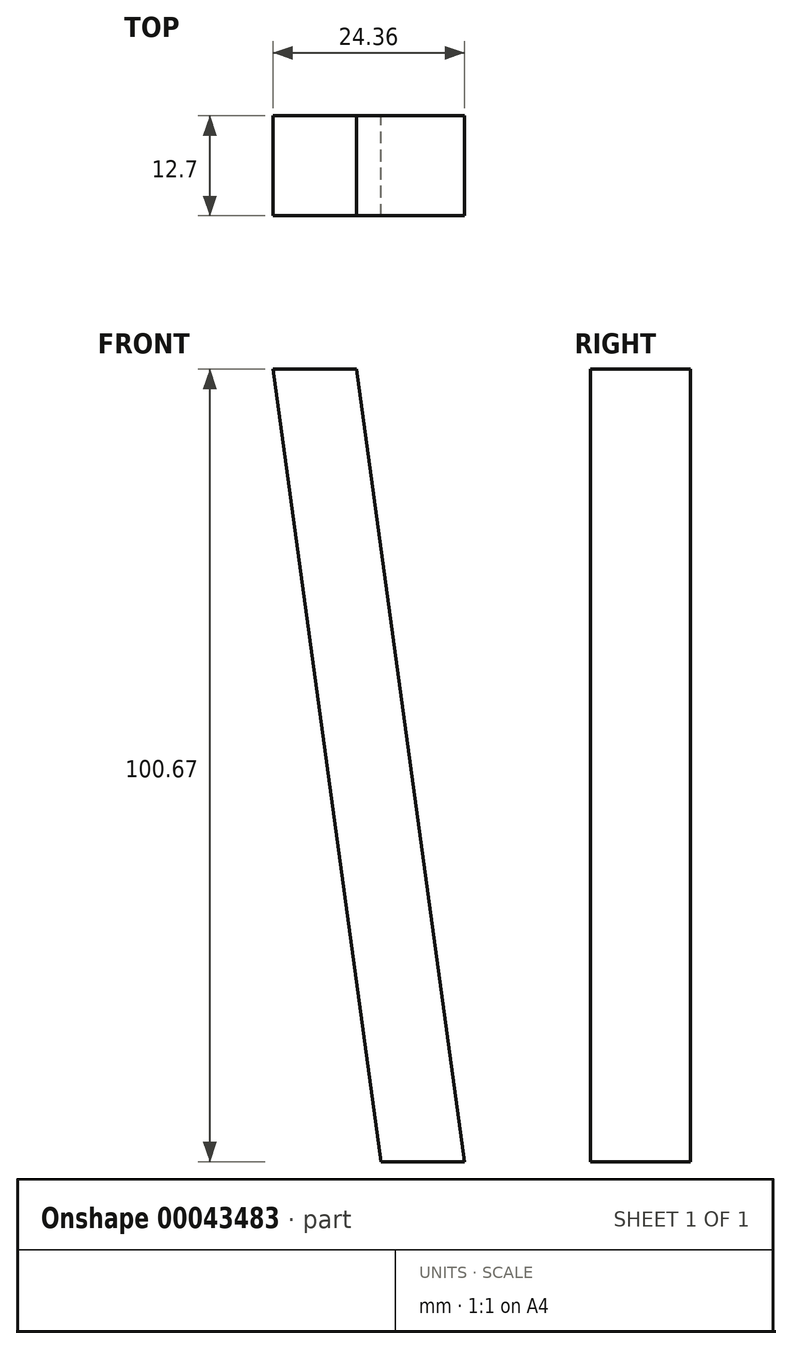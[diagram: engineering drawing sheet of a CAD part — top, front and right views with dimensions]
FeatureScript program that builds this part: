
annotation { "Feature Type Name" : "Feature", "Feature Type Description" : "" }
export const myFeature = defineFeature(function(context is Context, id is Id, definition is map)
    precondition{}
    {
        {
            var Q0;
            Q0=qCreatedBy(makeId("Front.planeOp"),FACE);
            var sketch = newSketch(context, id + "F0", { "sketchPlane" : qUnion([Q0])});
            skLineSegment(sketch, "E0", {"start": v(13.13, 55.6) * mm, "end": v(23.77, 55.6) * mm});
            skLineSegment(sketch, "E1", {"start": v(23.77, 55.6) * mm, "end": v(37.5, -45.06) * mm});
            skLineSegment(sketch, "E2", {"start": v(37.5, -45.06) * mm, "end": v(26.85, -45.06) * mm});
            skLineSegment(sketch, "E3", {"start": v(26.85, -45.06) * mm, "end": v(13.13, 55.6) * mm});
            skSolve(sketch);
        }
        {
            var Q0;
            Q0=makeQuery(id+"F0.imprint","IMPRINT",FACE,{"disambiguationData":[TD([[makeQuery(id+"F0.imprint","IMPRINT",EDGE,{"derivedFrom":sQuery(id+"F0.wireOp",EDGE,"E0")}),-1.0]])]});
            extrude(context, id + "F1", {"entities" : qUnion([Q0]), "depth" : 12.7 * mm});
        }
    });
